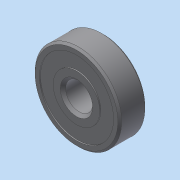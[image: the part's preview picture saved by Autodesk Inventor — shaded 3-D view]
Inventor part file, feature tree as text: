
AUTODESK INVENTOR PART (.ipt)
format: ipt  version: 2013 (Build 170138000, 138)  size: 130,048 bytes
history: native  units: mm
features: revolve x1, mirror x1, sketch x1
ambient origin geometry x8: Origin, YZ Plane, XZ Plane, XY Plane, X Axis, Y Axis, Z Axis, Center Point
bodies: Solid1 (feature_tree)
feature tree (3):
  revolve  "Revolution1"  [1 undecoded]
  mirror  "Mirror1"
  sketch  "Sketch1"  dims[d9=2.5mm d19=2.5mm d20=0.2mm d21=5.0mm d22=6.0mm d23=8.6mm d24=13.7mm d26=16.0mm d27=135.0deg d28=90.0deg d29=0.5mm d30=15.293mm]
note: 1 required parameter value undecoded (feature->parameter linkage not recoverable at this tier; creation-order binding heuristic only, values carry confidence <= 0.55)
